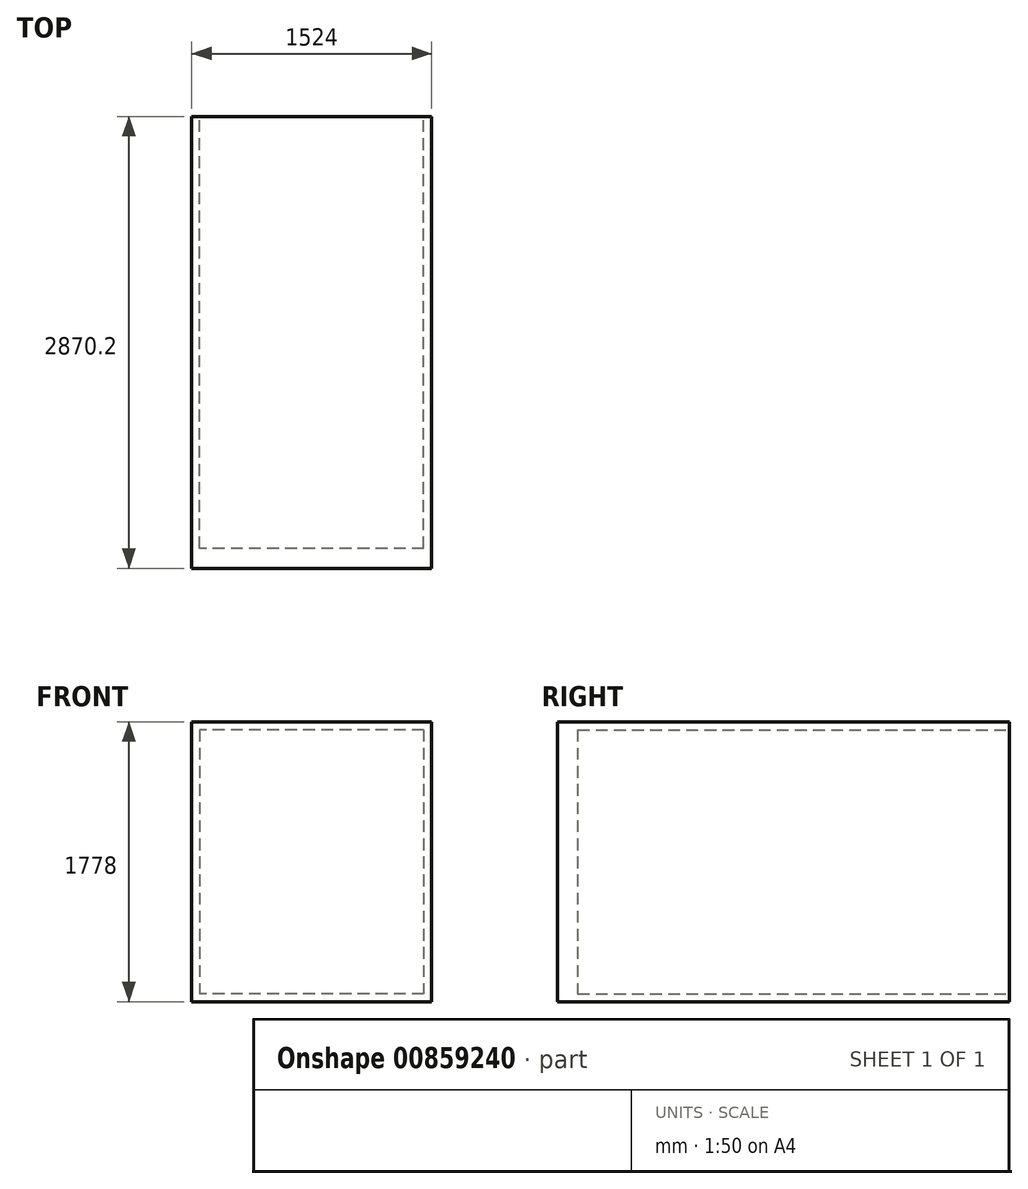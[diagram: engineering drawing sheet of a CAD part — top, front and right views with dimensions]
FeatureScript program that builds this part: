
annotation { "Feature Type Name" : "Feature", "Feature Type Description" : "" }
export const myFeature = defineFeature(function(context is Context, id is Id, definition is map)
    precondition{}
    {
        {
            var Q0;
            Q0=qCreatedBy(makeId("Front.planeOp"),FACE);
            var sketch = newSketch(context, id + "F0", { "sketchPlane" : qUnion([Q0])});
            skLineSegment(sketch, "E0.bottom", {"start": v(-762, 0) * mm, "end": v(762, 0) * mm});
            skLineSegment(sketch, "E0.top", {"start": v(-762, -1778) * mm, "end": v(762, -1778) * mm});
            skLineSegment(sketch, "E0.left", {"start": v(-762, 0) * mm, "end": v(-762, -1778) * mm});
            skLineSegment(sketch, "E0.right", {"start": v(762, 0) * mm, "end": v(762, -1778) * mm});
            skSolve(sketch);
        }
        {
            var Q0;
            Q0 = qSketchRegion(id + "F0", true);
            extrude(context, id + "F1", {"entities" : qUnion([Q0]), "depth" : 2870.2 * mm, "offsetDistance" : 25.4 * mm});
        }
        {
            var Q0;
            Q0=makeQuery(id+"F1.opExtrude","CAP_FACE",FACE,{"disambiguationData":[OSD([sQuery(id+"F0.wireOp",EDGE,"E0.bottom"),sQuery(id+"F0.wireOp",EDGE,"E0.top"),sQuery(id+"F0.wireOp",EDGE,"E0.left"),sQuery(id+"F0.wireOp",EDGE,"E0.right")])],"isStart":true});
            var sketch = newSketch(context, id + "F2", { "sketchPlane" : qUnion([Q0])});
            skLineSegment(sketch, "E1.bottom", {"start": v(-711.2, -50.8) * mm, "end": v(711.2, -50.8) * mm});
            skLineSegment(sketch, "E1.top", {"start": v(-711.2, -1727.2) * mm, "end": v(711.2, -1727.2) * mm});
            skLineSegment(sketch, "E1.left", {"start": v(-711.2, -50.8) * mm, "end": v(-711.2, -1727.2) * mm});
            skLineSegment(sketch, "E1.right", {"start": v(711.2, -50.8) * mm, "end": v(711.2, -1727.2) * mm});
            skPoint(sketch, "E2", {"position": v(0, -50.8) * mm});
            skSolve(sketch);
        }
        {
            var Q0;
            Q0 = qSketchRegion(id + "F2", true);
            extrude(context, id + "F3", {"entities" : qUnion([Q0]), "operationType" : NewBodyOperationType.REMOVE, "oppositeDirection" : true, "depth" : 2743.2 * mm, "offsetDistance" : 25.4 * mm});
        }
    });
